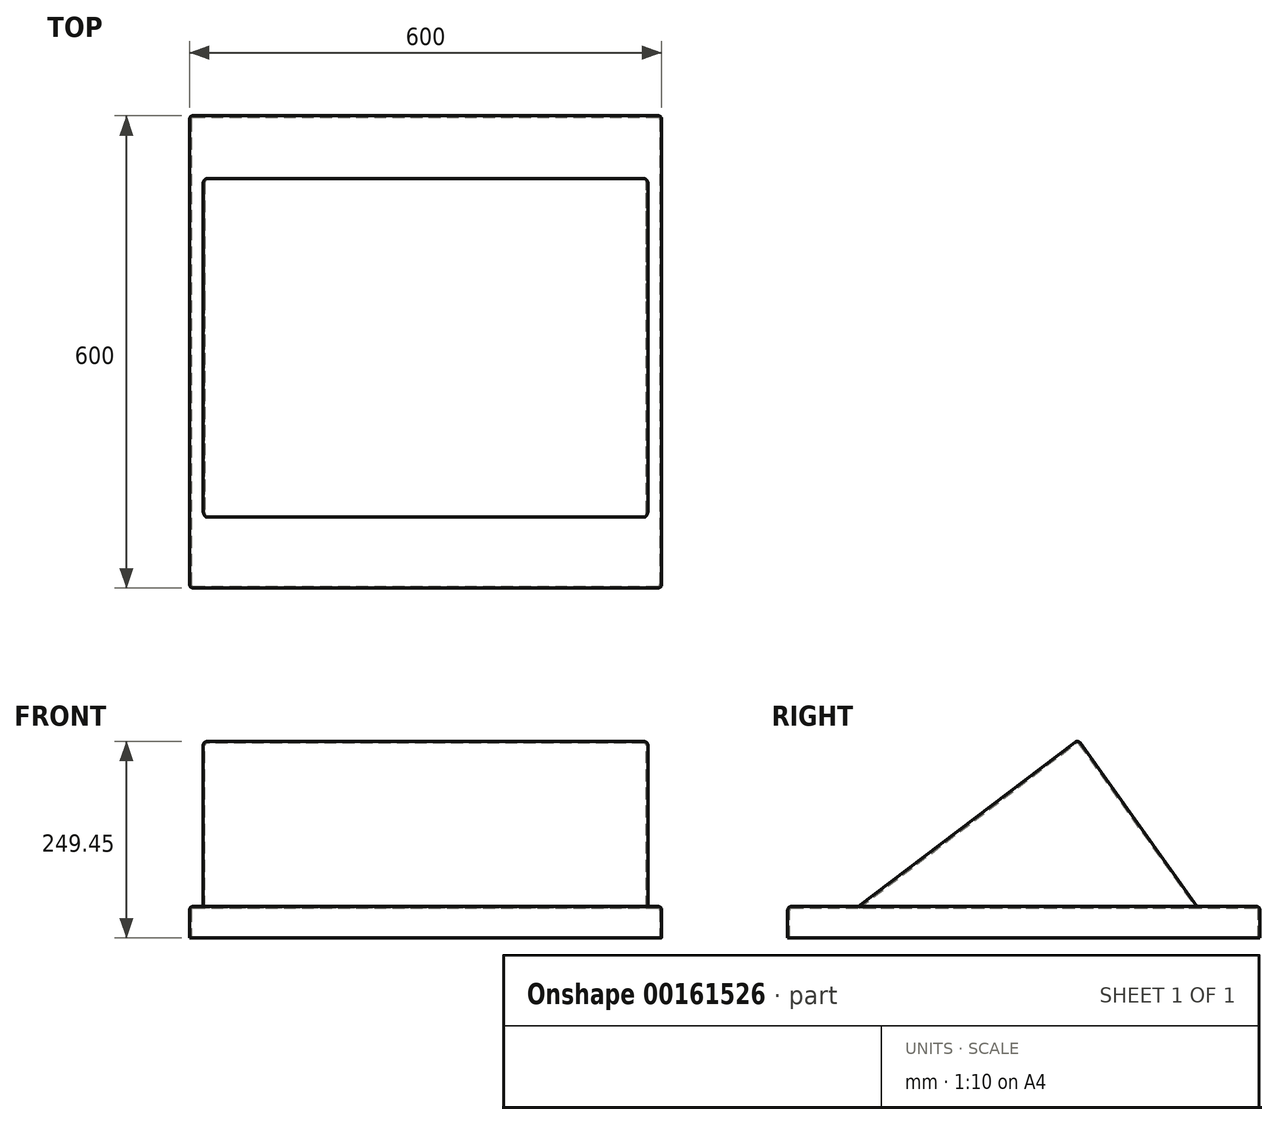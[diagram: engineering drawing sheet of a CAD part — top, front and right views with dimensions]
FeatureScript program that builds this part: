
annotation { "Feature Type Name" : "Feature", "Feature Type Description" : "" }
export const myFeature = defineFeature(function(context is Context, id is Id, definition is map)
    precondition{}
    {
        {
            var Q0;
            Q0=qCreatedBy(makeId("Top.planeOp"),FACE);
            var sketch = newSketch(context, id + "F0", { "sketchPlane" : qUnion([Q0])});
            skLineSegment(sketch, "E0.bottom", {"start": v(-300, 300) * mm, "end": v(300, 300) * mm});
            skLineSegment(sketch, "E0.top", {"start": v(-300, -300) * mm, "end": v(300, -300) * mm});
            skLineSegment(sketch, "E0.left", {"start": v(-300, 300) * mm, "end": v(-300, -300) * mm});
            skLineSegment(sketch, "E0.right", {"start": v(300, 300) * mm, "end": v(300, -300) * mm});
            skLineSegment(sketch, "E1", {"start": v(-300, -300) * mm, "end": v(300, 300) * mm, "construction": true});
            skSolve(sketch);
        }
        {
            var Q0;
            Q0 = qSketchRegion(id + "F0", true);
            extrude(context, id + "F1", {"entities" : qUnion([Q0]), "depth" : 40 * mm});
        }
        {
            var Q0;
            Q0=qCreatedBy(makeId("Right.planeOp"),FACE);
            var sketch = newSketch(context, id + "F2", { "sketchPlane" : qUnion([Q0])});
            skLineSegment(sketch, "E2", {"start": v(68.84, 251.54) * mm, "end": v(-210, 40) * mm});
            skLineSegment(sketch, "E3", {"start": v(-210, 40) * mm, "end": v(220, 40) * mm});
            skLineSegment(sketch, "E4", {"start": v(220, 40) * mm, "end": v(68.84, 251.54) * mm});
            skSolve(sketch);
        }
        {
            var Q0;
            Q0 = qSketchRegion(id + "F2", true);
            extrude(context, id + "F3", {"entities" : qUnion([Q0]), "operationType" : NewBodyOperationType.ADD, "endBound" : BoundingType.SYMMETRIC, "depth" : 565 * mm});
        }
        {
            var Q0;
            Q0=makeQuery(id+"F3.opExtrude","SWEPT_EDGE",EDGE,{"disambiguationData":[OSD([sQuery(id+"F2.wireOp",EDGE,"E2"),sQuery(id+"F2.wireOp",EDGE,"E3")])]});
            var Q1;
            Q1=makeQuery(id+"F3.opExtrude","CAP_EDGE",EDGE,{"disambiguationData":[OSD([sQuery(id+"F2.wireOp",EDGE,"E3")])],"isStart":false});
            var Q2;
            Q2=makeQuery(id+"F3.opExtrude","CAP_EDGE",EDGE,{"disambiguationData":[OSD([sQuery(id+"F2.wireOp",EDGE,"E2")])],"isStart":false});
            var Q3;
            Q3=makeQuery(id+"F3.opExtrude","CAP_EDGE",EDGE,{"disambiguationData":[OSD([sQuery(id+"F2.wireOp",EDGE,"E4")])],"isStart":false});
            var Q4;
            Q4=makeQuery(id+"F3.opExtrude","SWEPT_EDGE",EDGE,{"disambiguationData":[OSD([sQuery(id+"F2.wireOp",EDGE,"E2"),sQuery(id+"F2.wireOp",EDGE,"E4")])]});
            var Q5;
            Q5=makeQuery(id+"F1.opExtrude","CAP_EDGE",EDGE,{"disambiguationData":[OSD([sQuery(id+"F0.wireOp",EDGE,"E0.bottom")])],"isStart":false});
            var Q6;
            Q6=makeQuery(id+"F1.opExtrude","SWEPT_EDGE",EDGE,{"disambiguationData":[OSD([sQuery(id+"F0.wireOp",EDGE,"E0.bottom"),sQuery(id+"F0.wireOp",EDGE,"E0.right")])]});
            var Q7;
            Q7=makeQuery(id+"F1.opExtrude","SWEPT_EDGE",EDGE,{"disambiguationData":[OSD([sQuery(id+"F0.wireOp",EDGE,"E0.top"),sQuery(id+"F0.wireOp",EDGE,"E0.right")])]});
            var Q8;
            Q8=makeQuery(id+"F1.opExtrude","SWEPT_EDGE",EDGE,{"disambiguationData":[OSD([sQuery(id+"F0.wireOp",EDGE,"E0.top"),sQuery(id+"F0.wireOp",EDGE,"E0.left")])]});
            var Q9;
            Q9=makeQuery(id+"F1.opExtrude","SWEPT_EDGE",EDGE,{"disambiguationData":[OSD([sQuery(id+"F0.wireOp",EDGE,"E0.bottom"),sQuery(id+"F0.wireOp",EDGE,"E0.left")])]});
            var Q10;
            Q10=makeQuery(id+"F3.opExtrude","CAP_EDGE",EDGE,{"disambiguationData":[OSD([sQuery(id+"F2.wireOp",EDGE,"E4")])],"isStart":true});
            var Q11;
            Q11=makeQuery(id+"F3.opExtrude","CAP_EDGE",EDGE,{"disambiguationData":[OSD([sQuery(id+"F2.wireOp",EDGE,"E2")])],"isStart":true});
            var Q12;
            Q12=makeQuery(id+"F1.opExtrude","CAP_EDGE",EDGE,{"disambiguationData":[OSD([sQuery(id+"F0.wireOp",EDGE,"E0.top")])],"isStart":false});
            var Q13;
            Q13=makeQuery(id+"F1.opExtrude","CAP_EDGE",EDGE,{"disambiguationData":[OSD([sQuery(id+"F0.wireOp",EDGE,"E0.left")])],"isStart":false});
            var Q14;
            Q14=makeQuery(id+"F1.opExtrude","CAP_EDGE",EDGE,{"disambiguationData":[OSD([sQuery(id+"F0.wireOp",EDGE,"E0.right")])],"isStart":false});
            fillet(context, id + "F4", {"entities" : qUnion([Q0, Q1, Q2, Q3, Q4, Q5, Q6, Q7, Q8, Q9, Q10, Q11, Q12, Q13, Q14]), "radius" : 5 * mm, "tangentPropagation" : true, "allowEdgeOverflow" : false});
        }
        {
            var Q0;
            Q0=makeQuery(id+"F1.opExtrude","CAP_FACE",FACE,{"disambiguationData":[OSD([sQuery(id+"F0.wireOp",EDGE,"E0.bottom"),sQuery(id+"F0.wireOp",EDGE,"E0.top"),sQuery(id+"F0.wireOp",EDGE,"E0.left"),sQuery(id+"F0.wireOp",EDGE,"E0.right")])],"isStart":true});
            shell(context, id + "F5", {"entities" : qUnion([Q0]), "thickness" : 2 * mm});
        }
    });
